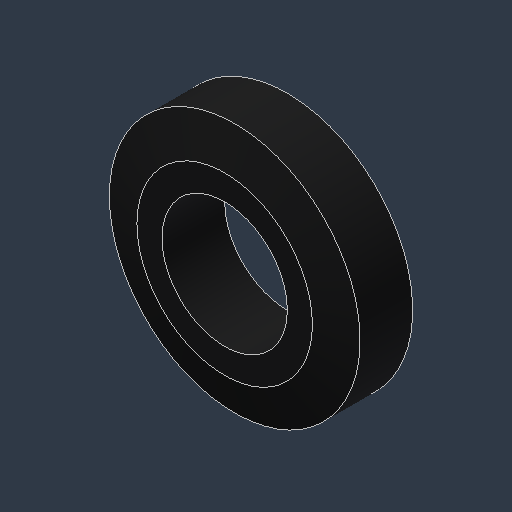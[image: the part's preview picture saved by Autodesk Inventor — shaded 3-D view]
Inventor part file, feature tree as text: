
AUTODESK INVENTOR PART (.ipt)
format: ipt  version: 2024.3 (Build 283343000, 343)  size: 100,352 bytes
history: native  units: mm (DEFAULTED — no unit token found)
features: revolve x1, sketch x1
ambient origin geometry x8: Origin, YZ Plane, XZ Plane, XY Plane, X Axis, Y Axis, Z Axis, Center Point
bodies: Solid1 (feature_tree)
feature tree (2):
  revolve  "Revolution1"  [1 undecoded]
  sketch  "Sketch2"  dims[d0=6.35mm d1=12.7mm d3=90.0deg d7=3.175mm d8=15.0deg d9=1.27mm]
note: 1 required parameter value undecoded (feature->parameter linkage not recoverable at this tier; creation-order binding heuristic only, values carry confidence <= 0.55)
